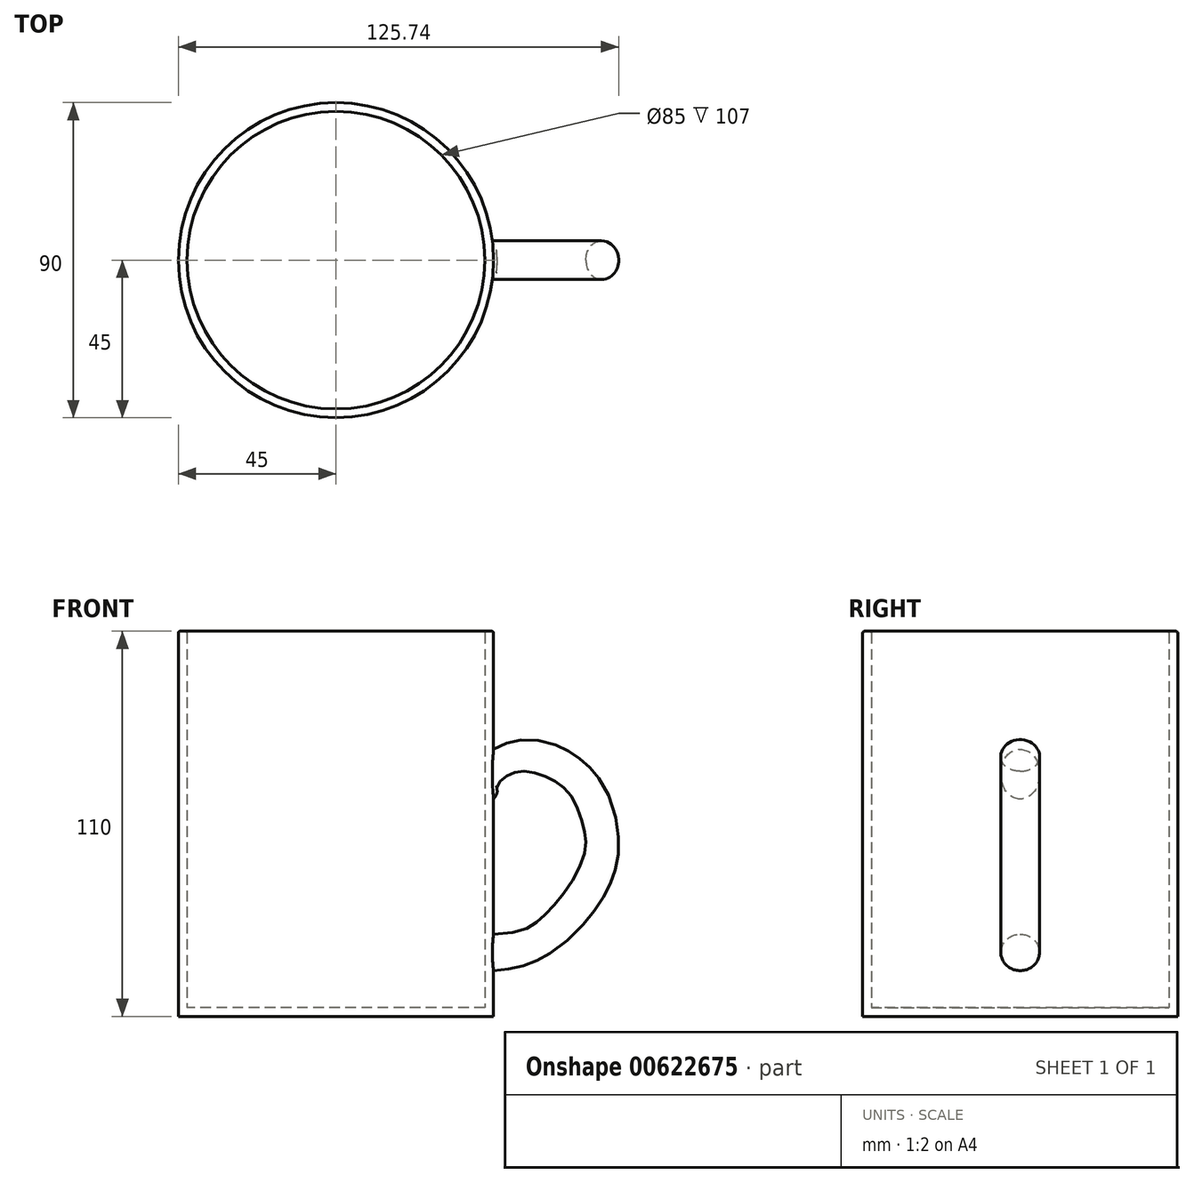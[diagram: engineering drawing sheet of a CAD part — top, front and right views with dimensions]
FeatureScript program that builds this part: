
annotation { "Feature Type Name" : "Feature", "Feature Type Description" : "" }
export const myFeature = defineFeature(function(context is Context, id is Id, definition is map)
    precondition{}
    {
        {
            var Q0;
            Q0=qCreatedBy(makeId("Top.planeOp"),FACE);
            var sketch = newSketch(context, id + "F0", { "sketchPlane" : qUnion([Q0])});
            skCircle(sketch, "E0", {"center": v(0, 0) * mm, "radius": 45 * mm});
            skSolve(sketch);
        }
        {
            var Q0;
            Q0=makeQuery(id+"F0.imprint","IMPRINT",FACE,{"disambiguationData":[TD([[makeQuery(id+"F0.imprint","IMPRINT",EDGE,{"derivedFrom":sQuery(id+"F0.wireOp",EDGE,"E0")}),1.0]])]});
            extrude(context, id + "F1", {"entities" : qUnion([Q0]), "depth" : 110 * mm, "offsetDistance" : 25 * mm});
        }
        {
            var Q0;
            Q0=qCreatedBy(makeId("Right.planeOp"),FACE);
            cPlane(context, id + "F2", {"entities" : qUnion([Q0]), "cplaneType" : CPlaneType.OFFSET, "offset" : 46 * mm, "width" : 150 * mm, "height" : 150 * mm});
        }
        {
            var Q0;
            Q0=qCreatedBy(id+"F2.planeOp",FACE);
            var sketch = newSketch(context, id + "F3", { "sketchPlane" : qUnion([Q0])});
            skCircle(sketch, "E1", {"center": v(0, 71.38) * mm, "radius": 5.52 * mm});
            skSolve(sketch);
        }
        {
            var Q0;
            Q0=qCreatedBy(makeId("Front.planeOp"),FACE);
            var sketch = newSketch(context, id + "F4", { "sketchPlane" : qUnion([Q0])});
            skFitSpline(sketch, "E2", {"points": [v(35.65, 78.59) * mm, v(43.96, 84.72) * mm, v(58.3, 86.83) * mm, v(73.83, 80.45) * mm, v(85.14, 66.7) * mm, v(88.72, 47.55) * mm, v(84.35, 31.9) * mm, v(72.34, 16.46) * mm, v(56.44, 6.92) * mm, v(39.48, 4.55) * mm], "startDerivative": vector(84.66, 78.07) * mm, "endDerivative": vector(-152.51, -8.29) * mm});
            skSolve(sketch);
        }
        {
            var Q0;
            Q0=makeQuery(id+"F3.imprint","IMPRINT",FACE,{"disambiguationData":[TD([[makeQuery(id+"F3.imprint","IMPRINT",EDGE,{"derivedFrom":sQuery(id+"F3.wireOp",EDGE,"E1")}),1.0]])]});
            var Q1;
            Q1=sQuery(id+"F4.wireOp",EDGE,"E2");
            sweep(context, id + "F5", {"operationType" : NewBodyOperationType.ADD, "profiles" : qUnion([Q0]), "path" : qUnion([Q1])});
        }
        {
            var Q0;
            Q0=makeQuery(id+"F1.opExtrude","CAP_FACE",FACE,{"disambiguationData":[OSD([sQuery(id+"F0.wireOp",EDGE,"E0")])],"isStart":false});
            shell(context, id + "F6", {"entities" : qUnion([Q0]), "thickness" : 2.5 * mm});
        }
        {
            var Q0;
            {var subQ0=sQuery(id+"F0.wireOp",EDGE,"E0");Q0=makeQuery(id+"F6.opShell","OFFSET_EDGE",EDGE,{"disambiguationData":[OSD([subQ0]),TDD([makeQuery(id+"F1.opExtrude","CAP_EDGE",EDGE,{"disambiguationData":[OSD([subQ0])],"isStart":false})])]});}
            var Q1;
            Q1=makeQuery(id+"F1.opExtrude","CAP_EDGE",EDGE,{"disambiguationData":[OSD([sQuery(id+"F0.wireOp",EDGE,"E0")])],"isStart":false});
            fillet(context, id + "F7", {"entities" : qUnion([Q0, Q1]), "radius" : 0.5 * mm, "tangentPropagation" : true, "allowEdgeOverflow" : false});
        }
    });
